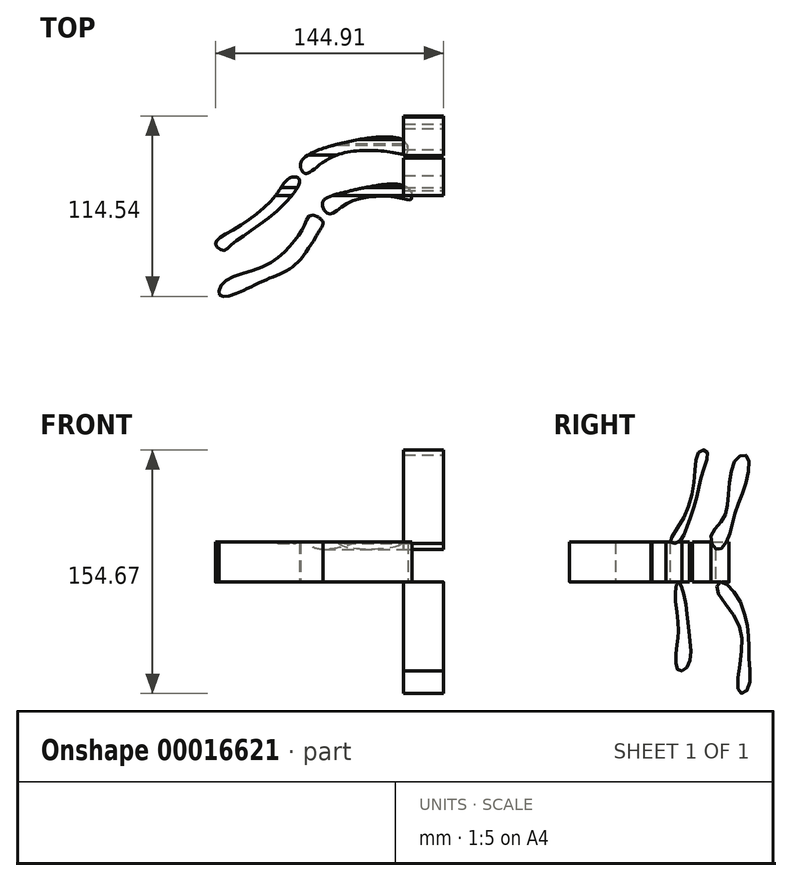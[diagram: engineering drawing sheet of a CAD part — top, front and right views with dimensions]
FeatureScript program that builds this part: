
annotation { "Feature Type Name" : "Feature", "Feature Type Description" : "" }
export const myFeature = defineFeature(function(context is Context, id is Id, definition is map)
    precondition{}
    {
        {
            var Q0;
            Q0=qCreatedBy(makeId("Top.planeOp"),FACE);
            var sketch = newSketch(context, id + "F0", { "sketchPlane" : qUnion([Q0])});
            skLineSegment(sketch, "E0", {"start": v(0, 0) * mm, "end": v(58.25, 0) * mm});
            skLineSegment(sketch, "E1", {"start": v(58.25, 0) * mm, "end": v(58.25, 44.17) * mm});
            skFitSpline(sketch, "E2", {"points": [v(0, 0) * mm, v(58.25, 44.17) * mm], "startDerivative": vector(20.16, 0) * mm, "endDerivative": vector(28.8, 91.21) * mm});
            skFitSpline(sketch, "E3", {"points": [v(58.25, 44.17) * mm, v(116.5, 61.77) * mm], "startDerivative": vector(55.69, 74.89) * mm, "endDerivative": vector(30.72, 8.64) * mm});
            skFitSpline(sketch, "E4", {"points": [v(-0.37, 28.3) * mm, v(43, 68.28) * mm], "startDerivative": vector(-4.64, 6.3) * mm, "endDerivative": vector(27.64, 64.88) * mm});
            skFitSpline(sketch, "E5", {"points": [v(43.86, 69.3) * mm, v(112.58, 91.9) * mm], "startDerivative": vector(56.1, 88.88) * mm, "endDerivative": vector(27.82, 6.05) * mm});
            skFitSpline(sketch, "E6", {"points": [v(0, 5.17) * mm, v(27.66, 16.35) * mm, v(44.27, 30.85) * mm, v(51.52, 41.72) * mm, v(55.15, 47.76) * mm, v(62.7, 44.17) * mm, v(60.58, 37.5) * mm, v(45.78, 16.65) * mm, v(27.96, 7.28) * mm, v(5.9, -2.68) * mm, v(-2.55, -2.68) * mm, v(0, 5.17) * mm]});
            skFitSpline(sketch, "E7", {"points": [v(-4.67, 31.45) * mm, v(10.74, 41.42) * mm, v(32.8, 60.15) * mm, v(40.04, 70.12) * mm, v(45.8, 72.12) * mm, v(48.2, 69.3) * mm, v(30.68, 47.76) * mm, v(5.6, 29.64) * mm, v(-0.37, 25.4) * mm, v(-4.67, 28.3) * mm, v(-4.67, 31.45) * mm]});
            skFitSpline(sketch, "E8", {"points": [v(62.7, 55.62) * mm, v(76.3, 62.26) * mm, v(116.5, 65.59) * mm, v(119.19, 58.03) * mm, v(111.63, 58.89) * mm, v(79.61, 55.92) * mm, v(66.62, 48.67) * mm, v(62.7, 55.62) * mm]});
            skFitSpline(sketch, "E9", {"points": [v(51.82, 74.35) * mm, v(69.65, 85.22) * mm, v(110.73, 87.03) * mm, v(116.17, 86.73) * mm, v(115.26, 94.58) * mm, v(68.44, 91.9) * mm, v(48.8, 80.39) * mm, v(51.82, 74.35) * mm]});
            skSolve(sketch);
        }
        {
            var Q0;
            Q0=makeQuery(id+"F0.imprint","IMPRINT",FACE,{"disambiguationData":[TD([[makeQuery(id+"F0.imprint","IMPRINT",EDGE,{"derivedFrom":sQuery(id+"F0.wireOp",EDGE,"E9")}),1.0]])]});
            var Q1;
            Q1=makeQuery(id+"F0.imprint","IMPRINT",FACE,{"disambiguationData":[TD([[makeQuery(id+"F0.imprint","IMPRINT",EDGE,{"derivedFrom":sQuery(id+"F0.wireOp",EDGE,"E8")}),-1.0]])]});
            var Q2;
            Q2=makeQuery(id+"F0.imprint","IMPRINT",FACE,{"disambiguationData":[TD([[makeQuery(id+"F0.imprint","IMPRINT",EDGE,{"derivedFrom":sQuery(id+"F0.wireOp",EDGE,"E7")}),-1.0]])]});
            var Q3;
            {var subQ5=sQuery(id+"F0.wireOp",EDGE,"E2");Q3=makeQuery(id+"F0.imprint","IMPRINT",FACE,{"disambiguationData":[TD([[makeQuery(id+"F0.imprint","IMPRINT",EDGE,{"derivedFrom":subQ5}),1.0]])]});}
            var Q4;
            {var subQ0=sQuery(id+"F0.wireOp",EDGE,"E2");Q4=makeQuery(id+"F0.imprint","IMPRINT",FACE,{"disambiguationData":[TD([[makeQuery(id+"F0.imprint","IMPRINT",EDGE,{"derivedFrom":subQ0}),-1.0]])]});}
            var Q5;
            {var subQ0=sQuery(id+"F0.wireOp",EDGE,"E6");var subQ3=sQuery(id+"F0.wireOp",EDGE,"E3");var subQ4=makeQuery(id+"F0.imprint","INTERSECT",VERTEX,{"derivedFrom":[subQ3,subQ0]});Q5=makeQuery(id+"F0.imprint","IMPRINT",FACE,{"disambiguationData":[TD([[makeQuery(id+"F0.imprint","IMPRINT",EDGE,{"disambiguationData":[TD([[subQ4,-1.0]])],"derivedFrom":subQ0}),-1.0]])]});}
            extrude(context, id + "F1", {"entities" : qUnion([Q0, Q1, Q2, Q3, Q4, Q5]), "depth" : 25.4 * mm});
        }
        {
            var Q0;
            Q0=qCreatedBy(makeId("Right.planeOp"),FACE);
            var sketch = newSketch(context, id + "F2", { "sketchPlane" : qUnion([Q0])});
            skFitSpline(sketch, "E10", {"points": [v(91.95, 0) * mm, v(101.85, -7.73) * mm, v(109.46, -30.19) * mm, v(110.22, -49.22) * mm, v(109.08, -68.63) * mm, v(104.13, -70.15) * mm, v(104.51, -50.74) * mm, v(102.99, -25.24) * mm, v(89.67, -4.69) * mm, v(91.95, 0) * mm]});
            skFitSpline(sketch, "E11", {"points": [v(95.76, 25.38) * mm, v(101.09, 43.27) * mm, v(108.32, 63.44) * mm, v(108.7, 80.18) * mm, v(102.23, 78.28) * mm, v(97.28, 57.73) * mm, v(93.47, 39.84) * mm, v(85.86, 28.8) * mm, v(89.67, 20.81) * mm, v(95.76, 25.38) * mm]});
            skFitSpline(sketch, "E12", {"points": [v(60.36, 25.38) * mm, v(67.98, 39.46) * mm, v(75.59, 66.86) * mm, v(79.01, 83.23) * mm, v(83.58, 82.85) * mm, v(80.92, 70.67) * mm, v(76.73, 53.16) * mm, v(69.88, 32.6) * mm, v(65.31, 25.38) * mm, v(60.36, 25.38) * mm]});
            skFitSpline(sketch, "E13", {"points": [v(65.7, 0) * mm, v(69.88, -13.82) * mm, v(72.16, -32.85) * mm, v(71.4, -53.4) * mm, v(65.31, -56.07) * mm, v(64.17, -41.99) * mm, v(65.31, -28.67) * mm, v(63.4, -5.45) * mm, v(65.7, 0) * mm]});
            skSolve(sketch);
        }
        {
            var Q0;
            Q0=makeQuery(id+"F2.imprint","IMPRINT",FACE,{"disambiguationData":[TD([[makeQuery(id+"F2.imprint","IMPRINT",EDGE,{"derivedFrom":sQuery(id+"F2.wireOp",EDGE,"E11")}),1.0]])]});
            var Q1;
            Q1=makeQuery(id+"F2.imprint","IMPRINT",FACE,{"disambiguationData":[TD([[makeQuery(id+"F2.imprint","IMPRINT",EDGE,{"derivedFrom":sQuery(id+"F2.wireOp",EDGE,"E12")}),-1.0]])]});
            var Q2;
            Q2=makeQuery(id+"F2.imprint","IMPRINT",FACE,{"disambiguationData":[TD([[makeQuery(id+"F2.imprint","IMPRINT",EDGE,{"derivedFrom":sQuery(id+"F2.wireOp",EDGE,"E13")}),-1.0]])]});
            var Q3;
            Q3=makeQuery(id+"F2.imprint","IMPRINT",FACE,{"disambiguationData":[TD([[makeQuery(id+"F2.imprint","IMPRINT",EDGE,{"derivedFrom":sQuery(id+"F2.wireOp",EDGE,"E10")}),-1.0]])]});
            extrude(context, id + "F3", {"entities" : qUnion([Q0, Q1, Q2, Q3]), "depth" : 139.7 * mm});
        }
        {
            var Q0;
            Q0=makeQuery(id+"F3.opExtrude","CAP_FACE",FACE,{"disambiguationData":[OSD([sQuery(id+"F2.wireOp",EDGE,"E10")])],"isStart":true});
            var Q1;
            Q1=makeQuery(id+"F3.opExtrude","CAP_FACE",FACE,{"disambiguationData":[OSD([sQuery(id+"F2.wireOp",EDGE,"E11")])],"isStart":true});
            var Q2;
            Q2=makeQuery(id+"F3.opExtrude","CAP_FACE",FACE,{"disambiguationData":[OSD([sQuery(id+"F2.wireOp",EDGE,"E13")])],"isStart":true});
            var Q3;
            Q3=makeQuery(id+"F3.opExtrude","CAP_FACE",FACE,{"disambiguationData":[OSD([sQuery(id+"F2.wireOp",EDGE,"E12")])],"isStart":true});
            extrude(context, id + "F4", {"entities" : qUnion([Q0, Q1, Q2, Q3]), "operationType" : NewBodyOperationType.REMOVE, "oppositeDirection" : true, "depth" : 114.3 * mm});
        }
    });
